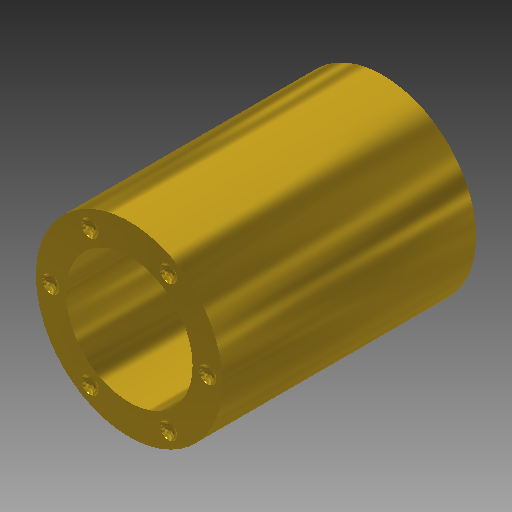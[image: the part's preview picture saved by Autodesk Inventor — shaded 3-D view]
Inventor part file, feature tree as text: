
AUTODESK INVENTOR PART (.ipt)
format: ipt  version: 2017 (Build 210142000, 142)  size: 195,584 bytes
history: native  units: mm (DEFAULTED — no unit token found)
features: revolve x2, pattern_circular x2, extrude x1, projected_geometry x1
ambient origin geometry x8: Origin, YZ Plane, XZ Plane, XY Plane, X Axis, Y Axis, Z Axis, Center Point
bodies: Solid1 (feature_tree)
feature tree (6):
  extrude  "Extrusion1"  Depth=12.7mm
  revolve  "Revolution2"  [1 undecoded]
  pattern_circular  "Circular Pattern1"  [2 undecoded]
  revolve  "Revolution3"  [1 undecoded]
  pattern_circular  "Circular Pattern2"  [2 undecoded]
  projected_geometry  "Projected Loop1"
note: 6 required parameter values undecoded (feature->parameter linkage not recoverable at this tier; creation-order binding heuristic only, values carry confidence <= 0.55)